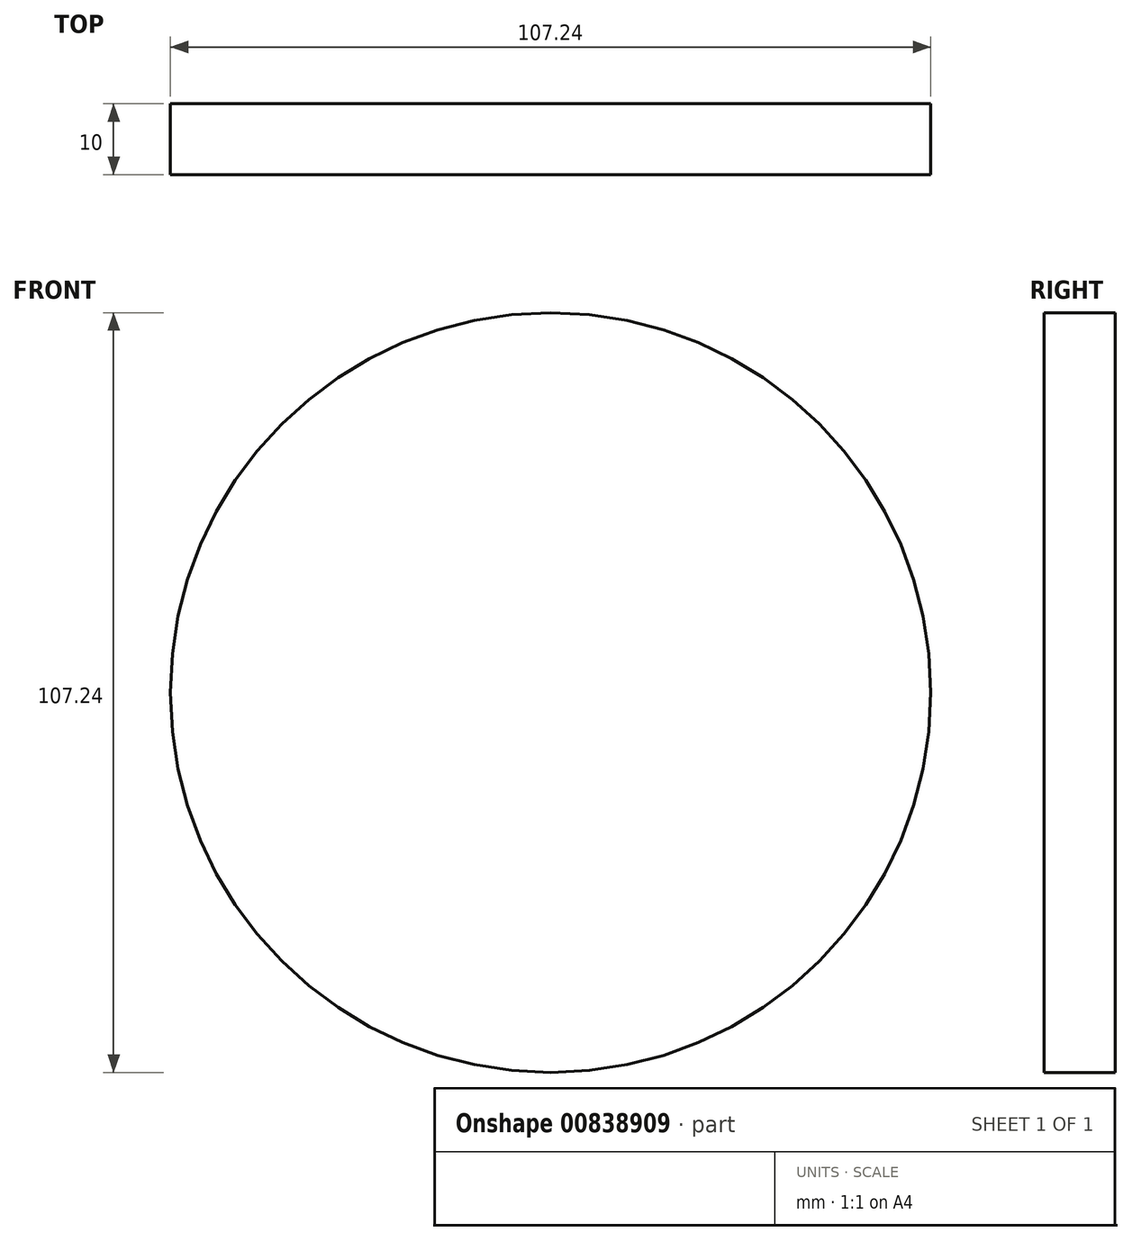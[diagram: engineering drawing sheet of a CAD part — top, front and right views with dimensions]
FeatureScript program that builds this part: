
annotation { "Feature Type Name" : "Feature", "Feature Type Description" : "" }
export const myFeature = defineFeature(function(context is Context, id is Id, definition is map)
    precondition{}
    {
        {
            var Q0;
            Q0=qCreatedBy(makeId("Front.planeOp"),FACE);
            var sketch = newSketch(context, id + "F0", { "sketchPlane" : qUnion([Q0])});
            skCircle(sketch, "E0", {"center": v(0, 0) * mm, "radius": 53.62 * mm});
            skSolve(sketch);
        }
        {
            var Q0;
            Q0=makeQuery(id+"F0.imprint","IMPRINT",FACE,{"disambiguationData":[TD([[makeQuery(id+"F0.imprint","IMPRINT",EDGE,{"derivedFrom":sQuery(id+"F0.wireOp",EDGE,"E0")}),1.0]])]});
            extrude(context, id + "F1", {"entities" : qUnion([Q0]), "depth" : 10 * mm, "offsetDistance" : 25.4 * mm});
        }
    });
